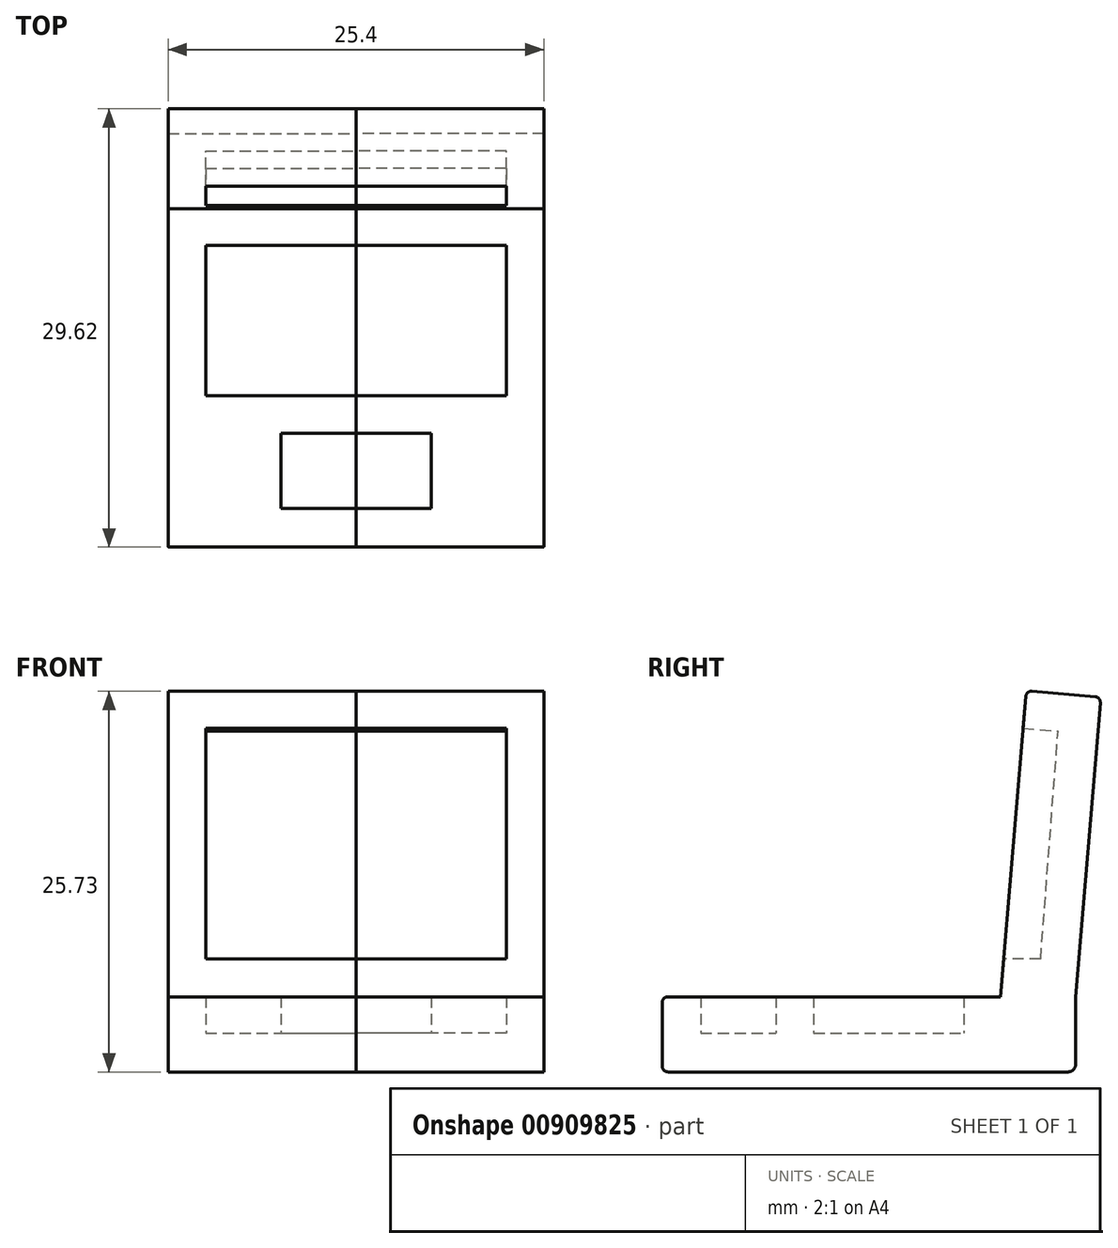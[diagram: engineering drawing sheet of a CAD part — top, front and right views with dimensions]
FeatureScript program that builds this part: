
annotation { "Feature Type Name" : "Feature", "Feature Type Description" : "" }
export const myFeature = defineFeature(function(context is Context, id is Id, definition is map)
    precondition{}
    {
        {
            var Q0;
            Q0=qCreatedBy(makeId("Right.planeOp"),FACE);
            var sketch = newSketch(context, id + "F0", { "sketchPlane" : qUnion([Q0])});
            skLineSegment(sketch, "E0.bottom", {"start": v(5.01, -2.62) * mm, "end": v(-17.46, -2.62) * mm});
            skLineSegment(sketch, "E0.top", {"start": v(5.01, 2.46) * mm, "end": v(-17.46, 2.46) * mm});
            skLineSegment(sketch, "E0.left", {"start": v(5.01, -2.62) * mm, "end": v(5.01, 2.46) * mm});
            skLineSegment(sketch, "E0.right", {"start": v(-17.85, -2.23) * mm, "end": v(-17.85, 2.08) * mm});
            skLineSegment(sketch, "E1", {"start": v(5.01, 2.46) * mm, "end": v(6.72, 22.76) * mm});
            skLineSegment(sketch, "E2", {"start": v(7.14, 23.11) * mm, "end": v(11.42, 22.75) * mm});
            skLineSegment(sketch, "E3", {"start": v(11.77, 22.34) * mm, "end": v(10.1, 2.46) * mm});
            skLineSegment(sketch, "E4", {"start": v(5.01, 2.46) * mm, "end": v(10.1, 2.46) * mm});
            skPoint(sketch, "E5.visualSharp", {"position": v(-17.85, -2.62) * mm});
            skArc(sketch, "E5.filletArc", {"start": v(-17.85, -2.23) * mm, "mid": v(-17.73, -2.5) * mm, "end": v(-17.46, -2.62) * mm});
            skPoint(sketch, "E6.visualSharp", {"position": v(-17.85, 2.46) * mm});
            skArc(sketch, "E6.filletArc", {"start": v(-17.46, 2.46) * mm, "mid": v(-17.73, 2.35) * mm, "end": v(-17.85, 2.08) * mm});
            skPoint(sketch, "E7.visualSharp", {"position": v(11.8, 22.72) * mm});
            skArc(sketch, "E7.filletArc", {"start": v(11.77, 22.34) * mm, "mid": v(11.68, 22.62) * mm, "end": v(11.42, 22.75) * mm});
            skPoint(sketch, "E8.visualSharp", {"position": v(6.75, 23.14) * mm});
            skArc(sketch, "E8.filletArc", {"start": v(7.14, 23.11) * mm, "mid": v(6.86, 23.02) * mm, "end": v(6.72, 22.76) * mm});
            skLineSegment(sketch, "E9.top", {"start": v(5.01, -2.62) * mm, "end": v(9.59, -2.62) * mm});
            skLineSegment(sketch, "E9.left", {"start": v(5.01, 2.46) * mm, "end": v(5.01, -2.62) * mm});
            skLineSegment(sketch, "E9.right", {"start": v(10.1, 2.46) * mm, "end": v(10.1, -2.1) * mm});
            skPoint(sketch, "E10.visualSharp", {"position": v(10.1, -2.62) * mm});
            skArc(sketch, "E10.filletArc", {"start": v(9.59, -2.62) * mm, "mid": v(9.95, -2.47) * mm, "end": v(10.1, -2.1) * mm});
            skSolve(sketch);
        }
        {
            var Q0;
            Q0 = qSketchRegion(id + "F0", true);
            extrude(context, id + "F1", {"entities" : qUnion([Q0]), "depth" : 12.7 * mm, "offsetDistance" : 25.4 * mm});
        }
        {
            var Q0;
            Q0=qCreatedBy(makeId("Right.planeOp"),FACE);
            var sketch = newSketch(context, id + "F2", { "sketchPlane" : qUnion([Q0])});
            skLineSegment(sketch, "E11.bottom", {"start": v(-7.62, 2.46) * mm, "end": v(2.54, 2.46) * mm});
            skLineSegment(sketch, "E11.top", {"start": v(-7.62, 0) * mm, "end": v(2.54, 0) * mm});
            skLineSegment(sketch, "E11.left", {"start": v(-7.62, 2.46) * mm, "end": v(-7.62, 0) * mm});
            skLineSegment(sketch, "E11.right", {"start": v(2.54, 2.46) * mm, "end": v(2.54, 0) * mm});
            skLineSegment(sketch, "E12", {"start": v(7.74, 5) * mm, "end": v(5.19, 5) * mm});
            skLineSegment(sketch, "E13", {"start": v(5.19, 5) * mm, "end": v(6.5, 20.6) * mm});
            skLineSegment(sketch, "E14", {"start": v(7.74, 5) * mm, "end": v(8.9, 20.41) * mm});
            skLineSegment(sketch, "E15", {"start": v(6.5, 20.6) * mm, "end": v(8.9, 20.41) * mm});
            skSolve(sketch);
        }
        {
            var Q0;
            Q0=makeQuery(id+"F2.imprint","IMPRINT",FACE,{"disambiguationData":[TD([[makeQuery(id+"F2.imprint","IMPRINT",EDGE,{"derivedFrom":sQuery(id+"F2.wireOp",EDGE,"E11.bottom")}),-1.0]])]});
            var Q1;
            Q1=makeQuery(id+"F2.imprint","IMPRINT",FACE,{"disambiguationData":[TD([[makeQuery(id+"F2.imprint","IMPRINT",EDGE,{"derivedFrom":sQuery(id+"F2.wireOp",EDGE,"E12")}),-1.0]])]});
            extrude(context, id + "F3", {"entities" : qUnion([Q0, Q1]), "operationType" : NewBodyOperationType.REMOVE, "depth" : 10.16 * mm, "offsetDistance" : 25.4 * mm});
        }
        {
            var Q0;
            Q0=qCreatedBy(makeId("Right.planeOp"),FACE);
            var sketch = newSketch(context, id + "F4", { "sketchPlane" : qUnion([Q0])});
            skLineSegment(sketch, "E16.bottom", {"start": v(-15.25, 2.53) * mm, "end": v(-10.17, 2.53) * mm});
            skLineSegment(sketch, "E16.top", {"start": v(-15.25, 0) * mm, "end": v(-10.17, 0) * mm});
            skLineSegment(sketch, "E16.left", {"start": v(-15.25, 2.53) * mm, "end": v(-15.25, 0) * mm});
            skLineSegment(sketch, "E16.right", {"start": v(-10.17, 2.53) * mm, "end": v(-10.17, 0) * mm});
            skSolve(sketch);
        }
        {
            var Q0;
            Q0 = qSketchRegion(id + "F4", true);
            var Q1;
            Q1 = qConstructionFilter(qBodyType(qCreatedBy(id + "F4" ,EDGE), BodyType.WIRE), ConstructionObject.NO);
            extrude(context, id + "F5", {"entities" : qUnion([Q0]), "operationType" : NewBodyOperationType.REMOVE, "surfaceEntities" : qUnion([Q1]), "depth" : 5.08 * mm, "offsetDistance" : 25.4 * mm});
        }
        {
            var Q0;
            Q0=makeQuery(id+"F1.opExtrude","SWEPT_BODY",BODY,{"disambiguationData":[OSD([sQuery(id+"F0.wireOp",EDGE,"E1"),sQuery(id+"F0.wireOp",EDGE,"E2"),sQuery(id+"F0.wireOp",EDGE,"E3"),sQuery(id+"F0.wireOp",EDGE,"E4")])]});
            var Q1;
            Q1=makeQuery(id+"F1.opExtrude","SWEPT_BODY",BODY,{"disambiguationData":[OSD([sQuery(id+"F0.wireOp",EDGE,"E0.bottom"),sQuery(id+"F0.wireOp",EDGE,"E0.top"),sQuery(id+"F0.wireOp",EDGE,"E0.left"),sQuery(id+"F0.wireOp",EDGE,"E0.right")])]});
            var Q2;
            Q2=makeQuery(id+"F5.opExtrude","SWEPT_BODY",BODY,{"disambiguationData":[OSD([sQuery(id+"F4.wireOp",EDGE,"E16.right")])]});
            var Q3;
            Q3=makeQuery(id+"FVubmRF0wqAMcug_2.opExtrude","SWEPT_BODY",BODY,{"disambiguationData":[OSD([sQuery(id+"FWncXGbdS2F7YQS_2.wireOp",EDGE,"wAtmCL0w-VAQV-DP8a-fyWK-mwNKCnr9ytpz.left")])]});
            var Q4;
            Q4=makeQuery(id+"FVubmRF0wqAMcug_2.opExtrude","SWEPT_BODY",BODY,{"disambiguationData":[OSD([sQuery(id+"FWncXGbdS2F7YQS_2.wireOp",EDGE,"HrcE8Ydu-QJe5-tlPE-bwSP-VmfstbeaMSJ1.right")])]});
            var Q5;
            Q5=qCreatedBy(makeId("Right.planeOp"),FACE);
            mirror(context, id + "F6", {"entities" : qUnion([Q0, Q1, Q2, Q3, Q4]), "mirrorPlane" : qUnion([Q5])});
        }
    });
